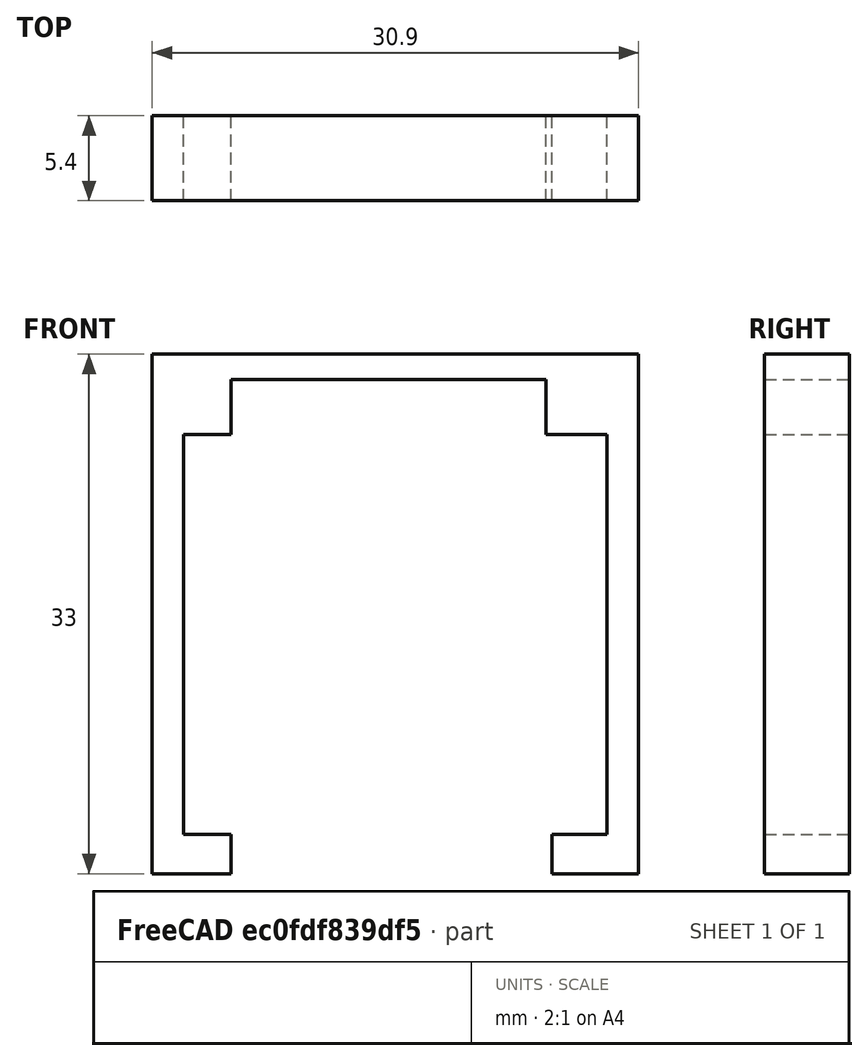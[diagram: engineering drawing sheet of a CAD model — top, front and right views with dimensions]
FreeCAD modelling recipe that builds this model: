
FCSTD DOCUMENT  (FreeCAD 0.18R16146 (Git))
Label: CableClip
License: All rights reserved
LicenseURL: http://en.wikipedia.org/wiki/All_rights_reserved
objects: Part::Box×4, App::MeasureDistance×4, Part::Cut×3
note: 7 computed .brp shape members not serialized (recipe doc carries the construction recipe); baked Part::Feature solids carry a one-line shape summary decoded from their .brp

FEATURE [Part::Box] Box  label="Cube"
  AttacherType = Attacher::AttachEngine3D
  Height = 33
  Length = 30.9
  Width = 5.4
FEATURE [Part::Box] Box001  label="Bar"
  AttacherType = Attacher::AttachEngine3D
  Height = 25.4
  Length = 26.9
  Placement = pos=(2,0,2.5) rot=(0,0,1;0rad)
  Width = 26
FEATURE [Part::Cut] Cut
  Base = -> Box
  Tool = -> Box001
FEATURE [Part::Box] Box002  label="Gap"
  AttacherType = Attacher::AttachEngine3D
  Height = 10
  Length = 20.4
  Placement = pos=(5,0,0) rot=(0,0,1;0rad)
  Width = 25.4
FEATURE [Part::Cut] Cut001
  Base = -> Cut
  Tool = -> Box002
FEATURE [Part::Box] Box003  label="CableSlot"
  AttacherType = Attacher::AttachEngine3D
  Height = 3.5
  Length = 20
  Placement = pos=(5,0,27.9) rot=(0,0,1;0rad)
  Width = 26
FEATURE [Part::Cut] Cut002
  Base = -> Cut001
  Placement = pos=(0,0,30) rot=(0,0,1;0rad)
  Tool = -> Box003
FEATURE [App::MeasureDistance] Distance  label="Distance: 2.96 mm"
  Distance = 2.96338
  P1 = (2.03662,0,32.5)
  P2 = (5,0,32.5)
FEATURE [App::MeasureDistance] Distance001  label="Distance: 4.98 mm"
  Distance = 4.97625
  P1 = (5,0,30)
  P2 = (0.0237508,0,30)
FEATURE [App::MeasureDistance] Distance002  label="Distance: 2.50 mm"
  Distance = 2.5
  P1 = (5,5.4,32.5)
  P2 = (5,5.4,30)
FEATURE [App::MeasureDistance] Distance003  label="Distance: 26.40 mm"
  Distance = 26.4003
  P1 = (2,0,57.7791)
  P2 = (28.4,0,57.9)
